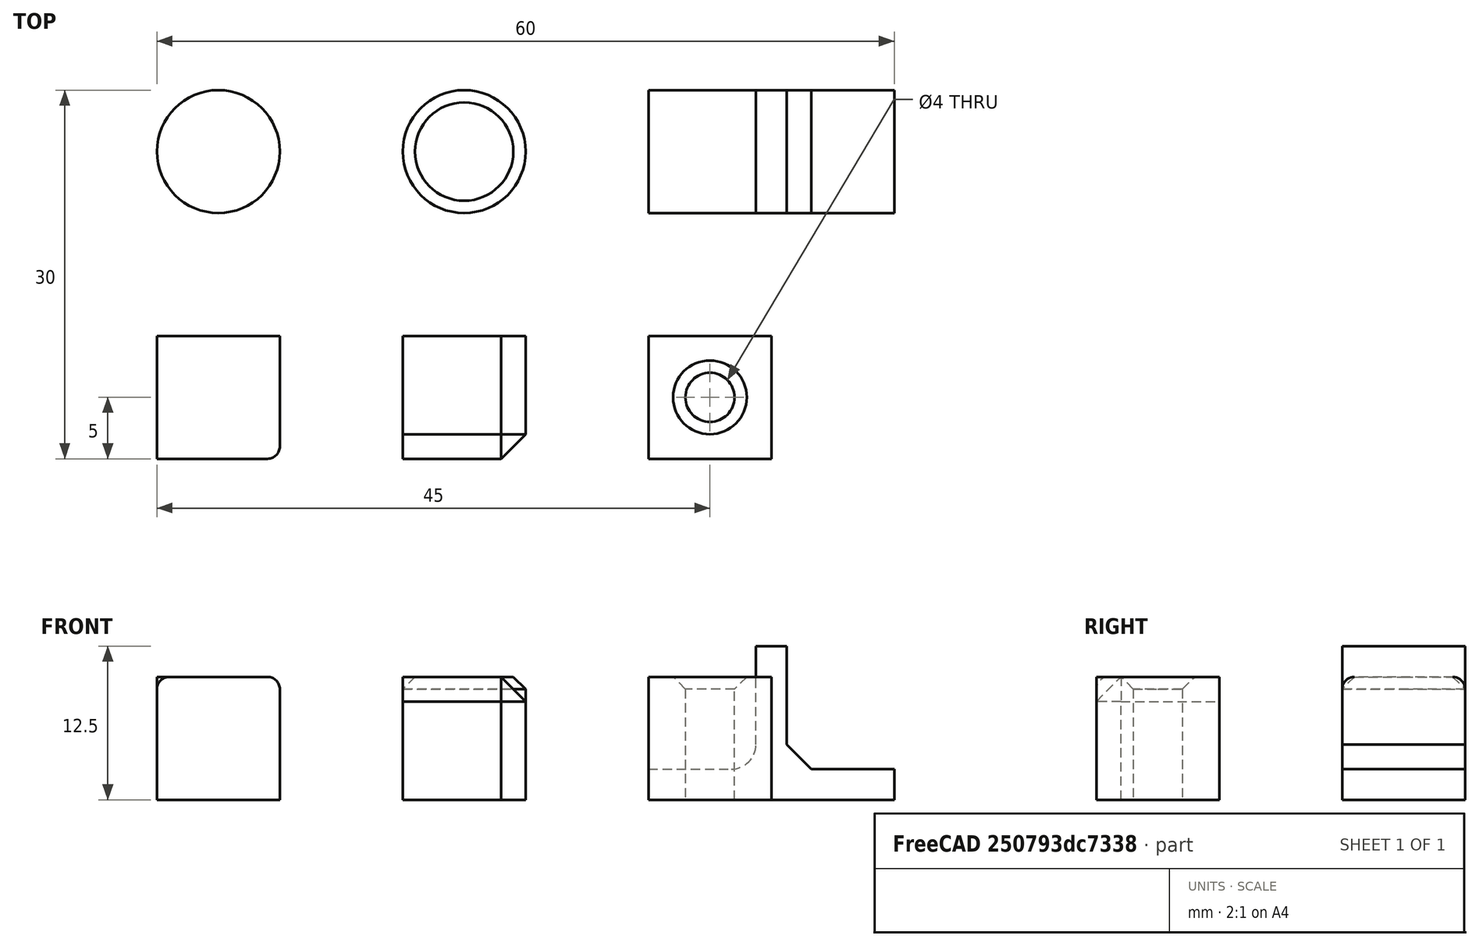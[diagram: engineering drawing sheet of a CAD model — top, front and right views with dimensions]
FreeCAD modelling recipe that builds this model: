
FCSTD DOCUMENT  (FreeCAD 1.0R39319 (Git))
Label: ojt1_t12p01_roundings_chamfers_reinforcements
License: All rights reserved
LicenseURL: https://en.wikipedia.org/wiki/All_rights_reserved
objects: Part::Box×5, Part::Chamfer×4, Part::Fillet×3, Part::Cylinder×3, Part::Cut×1, Part::MultiFuse×1
note: 17 computed .brp shape members not serialized (recipe doc carries the construction recipe); baked Part::Feature solids carry a one-line shape summary decoded from their .brp

FEATURE [Part::Box] Box  label="Cube"
  AttacherType = Attacher::AttachEngine3D
  Height = 10
  Length = 10
  Width = 10
FEATURE [Part::Fillet] Fillet
  Base = -> Box
  EdgeLinks = -> Box [Edge5,Edge6,Edge10]
  Edges = 3 edges r=1: [Edge5,Edge6,Edge10]
FEATURE [Part::Box] Box001  label="Cube001"
  AttacherType = Attacher::AttachEngine3D
  Height = 10
  Length = 10
  Placement = pos=(20,0,0) rot=(0,0,1;0rad)
  Width = 10
FEATURE [Part::Chamfer] Chamfer
  Base = -> Box001
  EdgeLinks = -> Box001 [Edge5,Edge6,Edge10]
  Edges = 3 edges r=2: [Edge5,Edge6,Edge10]
FEATURE [Part::Box] Box002  label="Cube002"
  AttacherType = Attacher::AttachEngine3D
  Height = 10
  Length = 10
  Placement = pos=(40,0,0) rot=(0,0,1;0rad)
  Width = 10
FEATURE [Part::Cylinder] Cylinder
  Angle = 360
  AttacherType = Attacher::AttachEngine3D
  FirstAngle = 0
  Height = 10
  Placement = pos=(45,5,0) rot=(0,0,1;0rad)
  Radius = 2
  SecondAngle = 0
FEATURE [Part::Cut] Cut
  Base = -> Box002
  Refine = true
  Tool = -> Cylinder
FEATURE [Part::Chamfer] Chamfer001
  Base = -> Cut
  EdgeLinks = -> Cut [Edge10]
  Edges = 1 edges r=1: [Edge10]
FEATURE [Part::Cylinder] Cylinder001
  Angle = 360
  AttacherType = Attacher::AttachEngine3D
  FirstAngle = 0
  Height = 10
  Placement = pos=(5,25,0) rot=(0,0,1;0rad)
  Radius = 5
  SecondAngle = 0
FEATURE [Part::Fillet] Fillet001
  Base = -> Cylinder001
  EdgeLinks = -> Cylinder001 [Edge3]
  Edges = 1 edges r=1: [Edge3]
FEATURE [Part::Cylinder] Cylinder002
  Angle = 360
  AttacherType = Attacher::AttachEngine3D
  FirstAngle = 0
  Height = 10
  Placement = pos=(25,25,0) rot=(0,0,1;0rad)
  Radius = 5
  SecondAngle = 0
FEATURE [Part::Chamfer] Chamfer002
  Base = -> Cylinder002
  EdgeLinks = -> Cylinder002 [Edge3]
  Edges = 1 edges r=1: [Edge3]
FEATURE [Part::Box] Box003  label="Cube003"
  AttacherType = Attacher::AttachEngine3D
  Height = 2.5
  Length = 20
  Placement = pos=(40,20,0) rot=(0,0,1;0rad)
  Width = 10
FEATURE [Part::Box] Box004  label="Cube004"
  AttacherType = Attacher::AttachEngine3D
  Height = 12.5
  Length = 2.5
  Placement = pos=(48.75,20,0) rot=(0,0,1;0rad)
  Width = 10
FEATURE [Part::MultiFuse] Fusion
  Refine = true
  Shapes = -> [Box004,Box003]
FEATURE [Part::Chamfer] Chamfer003
  Base = -> Fusion
  EdgeLinks = -> Fusion [Edge7]
  Edges = 1 edges r=2: [Edge7]
FEATURE [Part::Fillet] Fillet002
  Base = -> Chamfer003
  EdgeLinks = -> Chamfer003 [Edge25]
  Edges = 1 edges r=2: [Edge25]
